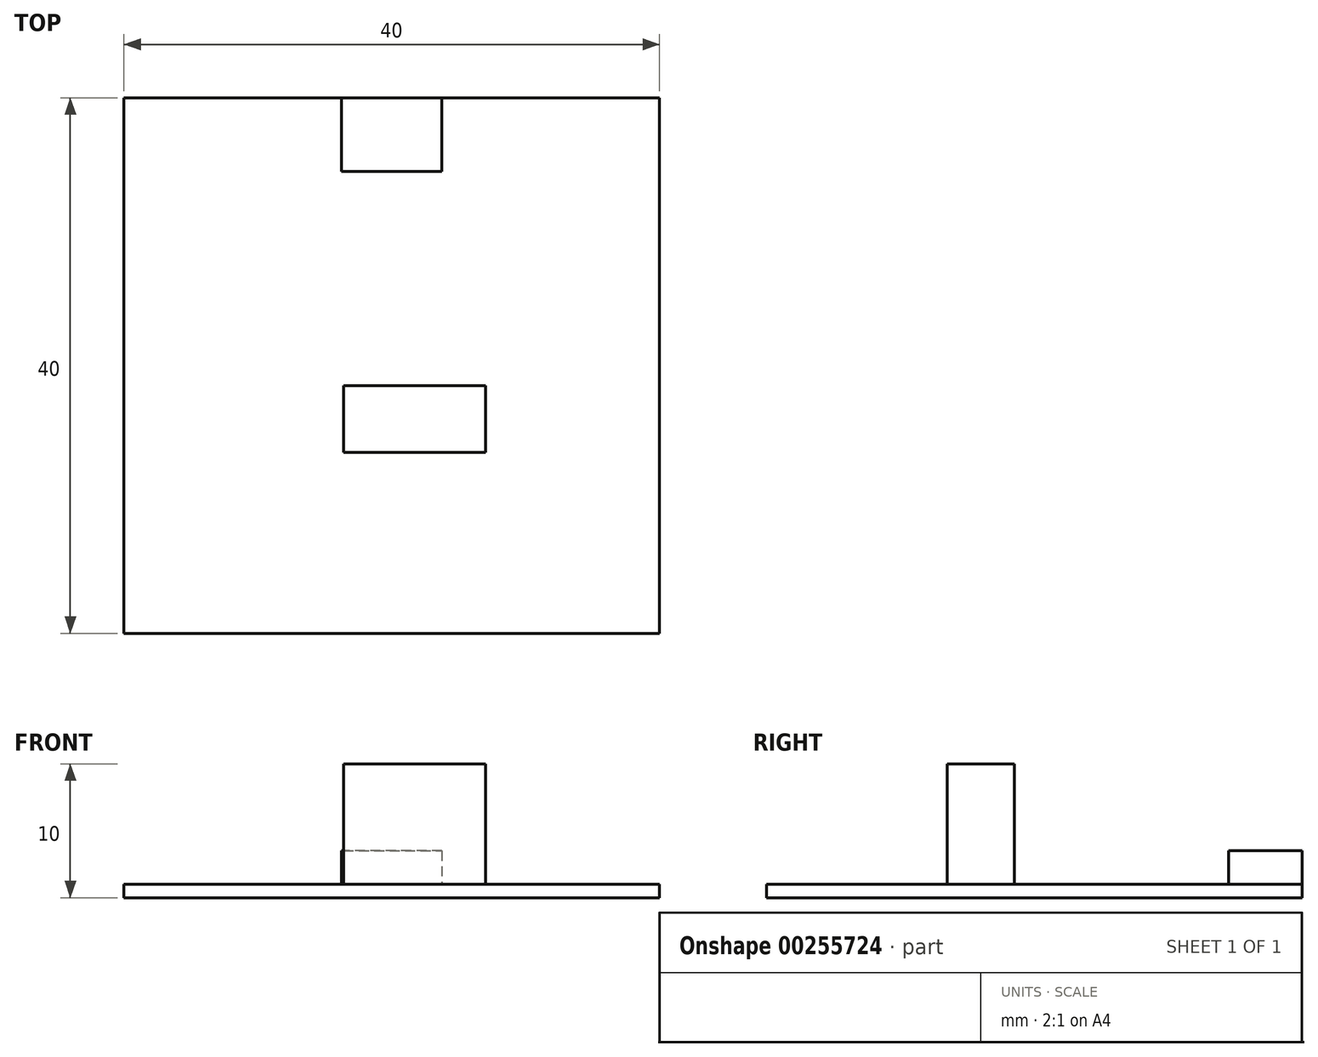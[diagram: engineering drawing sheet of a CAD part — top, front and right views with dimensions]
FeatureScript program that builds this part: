
annotation { "Feature Type Name" : "Feature", "Feature Type Description" : "" }
export const myFeature = defineFeature(function(context is Context, id is Id, definition is map)
    precondition{}
    {
        {
            var Q0;
            Q0=qCreatedBy(makeId("Top.planeOp"),FACE);
            var sketch = newSketch(context, id + "F0", { "sketchPlane" : qUnion([Q0])});
            skLineSegment(sketch, "E0.bottom", {"start": v(20, 20) * mm, "end": v(-20, 20) * mm});
            skLineSegment(sketch, "E0.top", {"start": v(20, -20) * mm, "end": v(-20, -20) * mm});
            skLineSegment(sketch, "E0.left", {"start": v(20, 20) * mm, "end": v(20, -20) * mm});
            skLineSegment(sketch, "E0.right", {"start": v(-20, 20) * mm, "end": v(-20, -20) * mm});
            skPoint(sketch, "E0.middle", {"position": v(0, 0) * mm});
            skSolve(sketch);
        }
        {
            var Q0;
            Q0=qSketchRegion(id+"F0",true);
            extrude(context, id + "F1", {"entities" : qUnion([Q0]), "depth" : 1 * mm});
        }
        {
            var Q0;
            Q0=makeQuery(id+"F1.opExtrude","CAP_FACE",FACE,{"disambiguationData":[OSD([sQuery(id+"F0.wireOp",EDGE,"E0.bottom"),sQuery(id+"F0.wireOp",EDGE,"E0.top"),sQuery(id+"F0.wireOp",EDGE,"E0.left"),sQuery(id+"F0.wireOp",EDGE,"E0.right")])],"isStart":false});
            var sketch = newSketch(context, id + "F2", { "sketchPlane" : qUnion([Q0])});
            skLineSegment(sketch, "E1.bottom", {"start": v(-3.6, -1.5) * mm, "end": v(7, -1.5) * mm});
            skLineSegment(sketch, "E1.top", {"start": v(-3.6, -6.5) * mm, "end": v(7, -6.5) * mm});
            skLineSegment(sketch, "E1.left", {"start": v(-3.6, -1.5) * mm, "end": v(-3.6, -6.5) * mm});
            skLineSegment(sketch, "E1.right", {"start": v(7, -1.5) * mm, "end": v(7, -6.5) * mm});
            skPoint(sketch, "E1.middle", {"position": v(1.7, -4) * mm});
            skLineSegment(sketch, "E2.bottom", {"start": v(-3.75, 20) * mm, "end": v(3.75, 20) * mm});
            skLineSegment(sketch, "E2.top", {"start": v(-3.75, 14.5) * mm, "end": v(3.75, 14.5) * mm});
            skLineSegment(sketch, "E2.left", {"start": v(-3.75, 20) * mm, "end": v(-3.75, 14.5) * mm});
            skLineSegment(sketch, "E2.right", {"start": v(3.75, 20) * mm, "end": v(3.75, 14.5) * mm});
            skPoint(sketch, "E2.middle", {"position": v(0, 17.25) * mm});
            skSolve(sketch);
        }
        {
            var Q0;
            Q0=makeQuery(id+"F2.imprint","IMPRINT",FACE,{"disambiguationData":[TD([[makeQuery(id+"F2.imprint","IMPRINT",EDGE,{"derivedFrom":sQuery(id+"F2.wireOp",EDGE,"E1.bottom")}),-1.0]])]});
            extrude(context, id + "F3", {"entities" : qUnion([Q0]), "operationType" : NewBodyOperationType.ADD, "depth" : 9 * mm});
        }
        {
            var Q0;
            Q0=makeQuery(id+"F2.imprint","IMPRINT",FACE,{"disambiguationData":[TD([[makeQuery(id+"F2.imprint","IMPRINT",EDGE,{"derivedFrom":sQuery(id+"F2.wireOp",EDGE,"E2.bottom")}),1.0]])]});
            extrude(context, id + "F4", {"entities" : qUnion([Q0]), "operationType" : NewBodyOperationType.ADD, "depth" : 2.5 * mm});
        }
    });
